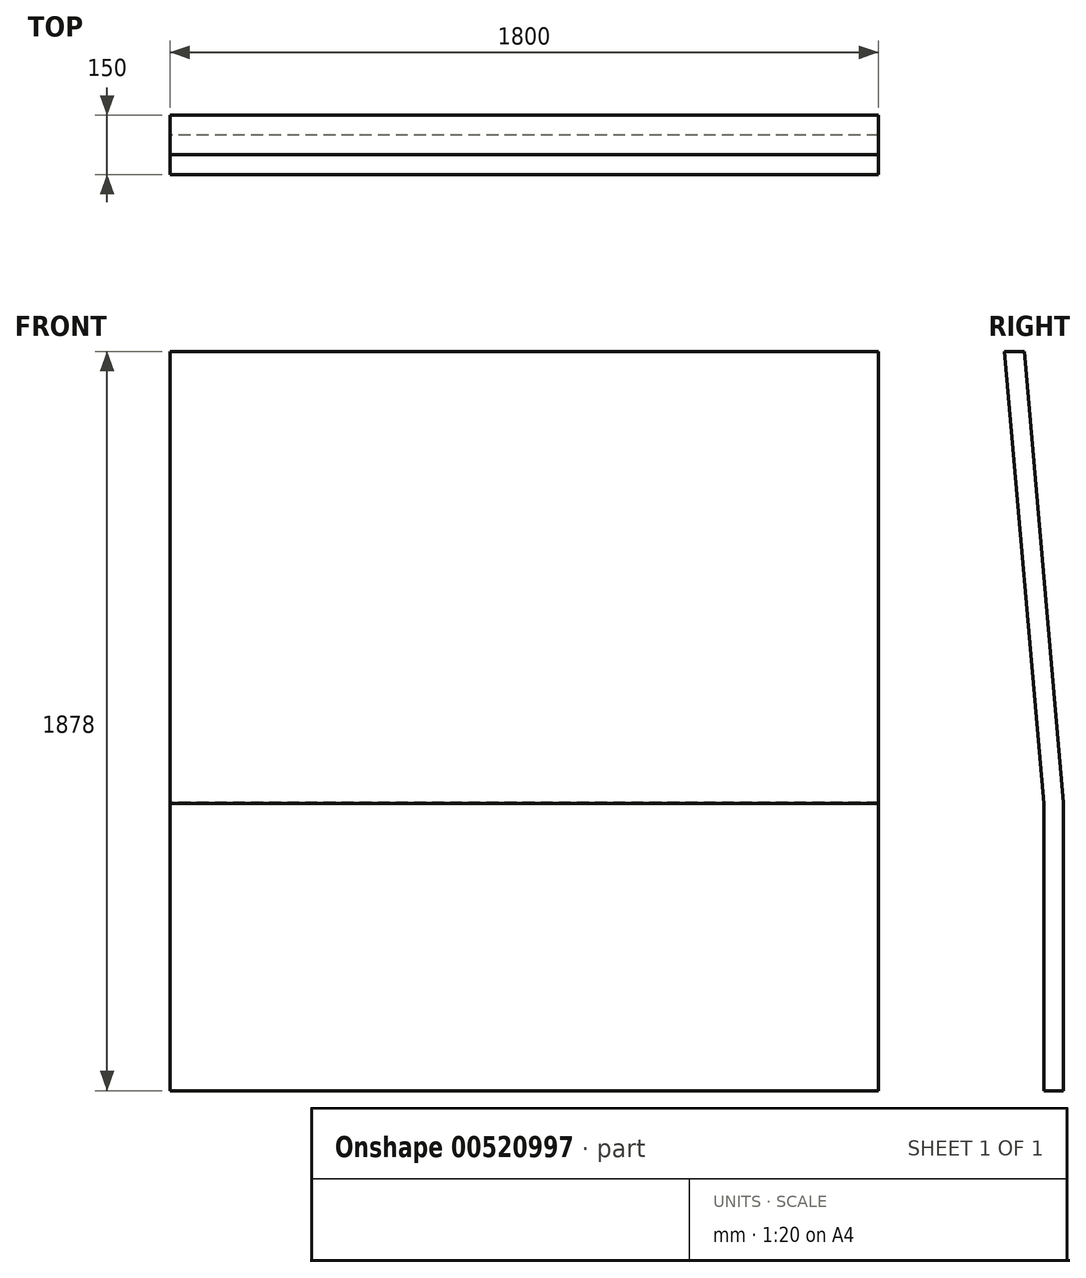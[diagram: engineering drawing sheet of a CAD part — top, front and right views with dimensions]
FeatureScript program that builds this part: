
annotation { "Feature Type Name" : "Feature", "Feature Type Description" : "" }
export const myFeature = defineFeature(function(context is Context, id is Id, definition is map)
    precondition{}
    {
        {
            var Q0;
            Q0=qCreatedBy(makeId("Right.planeOp"),FACE);
            var sketch = newSketch(context, id + "F0", { "sketchPlane" : qUnion([Q0])});
            skLineSegment(sketch, "E0", {"start": v(0, 0) * mm, "end": v(0, 730) * mm});
            skLineSegment(sketch, "E1", {"start": v(0, 730) * mm, "end": v(-100, 1878) * mm});
            skLineSegment(sketch, "E2.0", {"start": v(50, 732.17) * mm, "end": v(-49.81, 1878) * mm});
            skLineSegment(sketch, "E2.1", {"start": v(50, 0) * mm, "end": v(50, 732.17) * mm});
            skLineSegment(sketch, "E3", {"start": v(-100, 1878) * mm, "end": v(-49.81, 1878) * mm});
            skLineSegment(sketch, "E4", {"start": v(0, 0) * mm, "end": v(50, 0) * mm});
            skSolve(sketch);
        }
        {
            var Q0;
            Q0 = qSketchRegion(id + "F0", true);
            extrude(context, id + "F1", {"entities" : qUnion([Q0]), "depth" : 900 * mm, "offsetDistance" : 25 * mm, "hasSecondDirection" : true, "secondDirectionOppositeDirection" : true, "secondDirectionDepth" : 900 * mm});
        }
    });
